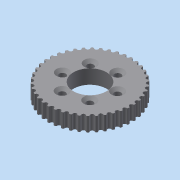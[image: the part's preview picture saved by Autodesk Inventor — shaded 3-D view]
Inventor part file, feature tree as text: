
AUTODESK INVENTOR PART (.ipt)
format: ipt  version: 2015 (Build 190159000, 159)  size: 1,331,200 bytes
history: native  units: in
note: dims shown in document units (in); Inventor stores cm internally (conversion verified against a paired STEP export)
features: projected_geometry x7, other x6, move_body x4, direct_edit x2, extrude x2, sketch x2, pattern_circular x1, split x1, chamfer x1, imported_body x1
ambient origin geometry x8: Origin, YZ Plane, XZ Plane, XY Plane, X Axis, Y Axis, Z Axis, Center Point
bodies: Solid1 (feature_tree)
feature tree (27):
  other  "WheelInsert.ipt"
  other  "a_6a24m042tm201"
  direct_edit  "Direct Edit1"
  direct_edit  "Direct Edit2"
  extrude  "Extrusion1"  Depth=16.5354in TaperAngle=360.0deg
  pattern_circular  "Circular Pattern1"  Count=42 Angle=360.0deg
  move_body  "Move Body1"
  move_body  "Move Body2"
  split  "Split1"
  extrude  "Extrusion2"  Depth=0.3937in TaperAngle=0.0deg
  chamfer  "Chamfer1"  Distance=0.3937in
  imported_body  "Base1"
  sketch  "Sketch1"  dims[d0=0.0in d1=0.0in d2=-7.4567in d7=16.5354in d9=360.0deg]
  projected_geometry  "Projected Loop1"
  other  "TaggingFeature1"
  sketch  "Sketch3"  dims[d11=0.3937in d12=0.0in d13=16.5354in d14=360.0deg d16=0.0in d17=0.0in d18=0.0202in d19=0.3937in d3=2.15in d4=0.25in d5=0.0in d6=0.25in d42=0.1625in d46=0.0in d47=0.375in d48=0.375in d49=0.375in d50=0.375in d51=0.375in d52=0.375in d53=0.01in d54=0.0in d67=0.01in d68=0.01in d69=2.3622in d73=0.02in d74=0.0in d78=0.047in d81=0.15in d82=0.145in d83=0.05in d84=0.0in d85=0.05in d88=0.0197in d89=0.0197in d90=0.0in d91=0.0197in d94=0.0098in d97=2.0in d98=2.3622in d99=360.0deg d71=360.0deg d20=90.0deg d21=0.0in d22=-4.274in d23=0.0in d24=0.3937in d25=0.0in d26=0.0835in d27=0.0787in d28=45.0deg]
  projected_geometry  "Projected Loop2"
  projected_geometry  "Projected Loop3"
  projected_geometry  "Projected Loop4"
  projected_geometry  "Projected Loop5"
  projected_geometry  "Projected Loop6"
  projected_geometry  "Projected Loop7"
  move_body  "Move1"
  other  "Delete1"
  move_body  "Move2"
  other  "Solid1::WheelInsert.ipt"
  other  "Srf1"
